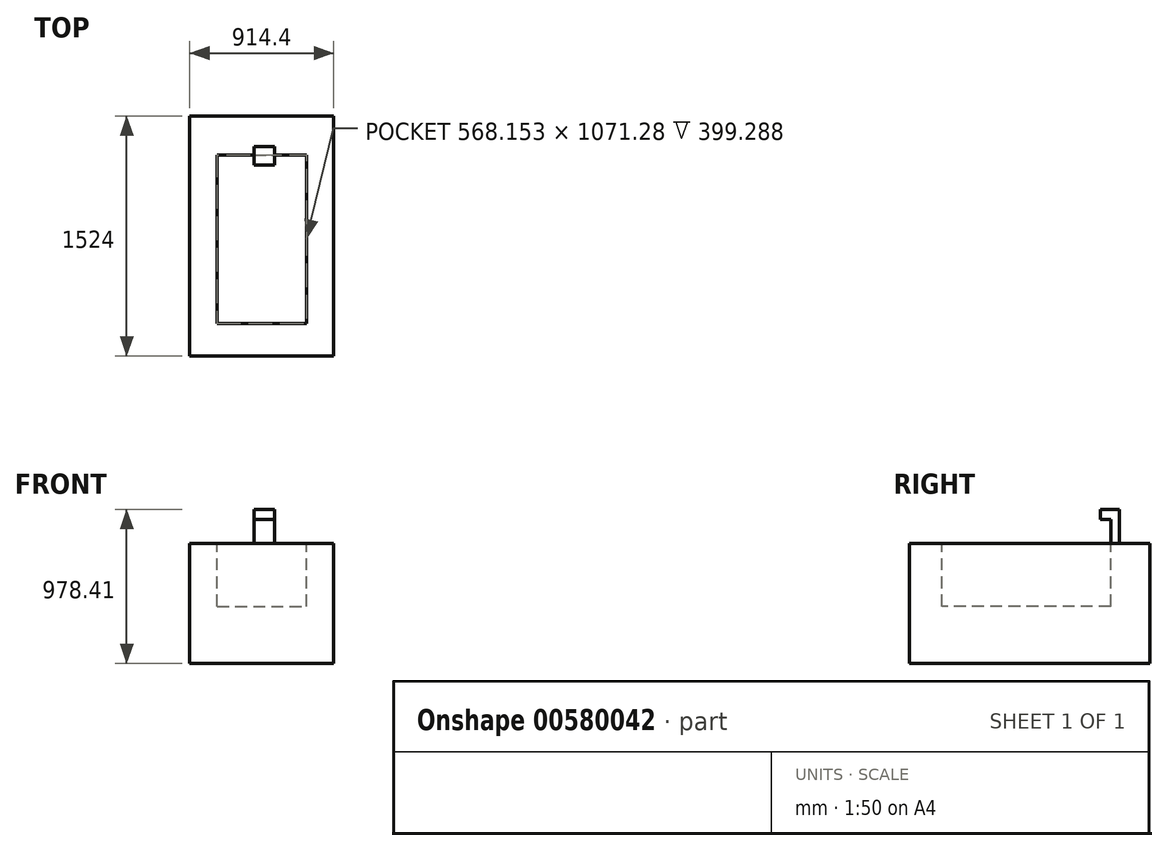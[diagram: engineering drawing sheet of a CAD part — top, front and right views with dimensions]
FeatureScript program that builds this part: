
annotation { "Feature Type Name" : "Feature", "Feature Type Description" : "" }
export const myFeature = defineFeature(function(context is Context, id is Id, definition is map)
    precondition{}
    {
        {
            var Q0;
            Q0=qCreatedBy(makeId("Top.planeOp"),FACE);
            var sketch = newSketch(context, id + "F0", { "sketchPlane" : qUnion([Q0])});
            skLineSegment(sketch, "E0.bottom", {"start": v(-580.76, 770.78) * mm, "end": v(333.64, 770.78) * mm});
            skLineSegment(sketch, "E0.top", {"start": v(-580.76, -753.22) * mm, "end": v(333.64, -753.22) * mm});
            skLineSegment(sketch, "E0.left", {"start": v(-580.76, 770.78) * mm, "end": v(-580.76, -753.22) * mm});
            skLineSegment(sketch, "E0.right", {"start": v(333.64, 770.78) * mm, "end": v(333.64, -753.22) * mm});
            skSolve(sketch);
        }
        {
            var Q0;
            Q0 = qSketchRegion(id + "F0", true);
            extrude(context, id + "F1", {"entities" : qUnion([Q0]), "depth" : 762 * mm, "offsetDistance" : 30.48 * mm});
        }
        {
            var Q0;
            Q0=makeQuery(id+"F1.opExtrude","CAP_FACE",FACE,{"disambiguationData":[OSD([sQuery(id+"F0.wireOp",EDGE,"E0.bottom"),sQuery(id+"F0.wireOp",EDGE,"E0.top"),sQuery(id+"F0.wireOp",EDGE,"E0.left"),sQuery(id+"F0.wireOp",EDGE,"E0.right")])],"isStart":false});
            var sketch = newSketch(context, id + "F2", { "sketchPlane" : qUnion([Q0])});
            skLineSegment(sketch, "E1.bottom", {"start": v(-407.14, 523.6) * mm, "end": v(161.01, 523.6) * mm});
            skLineSegment(sketch, "E1.top", {"start": v(-407.14, -547.67) * mm, "end": v(161.01, -547.67) * mm});
            skLineSegment(sketch, "E1.left", {"start": v(-407.14, 523.6) * mm, "end": v(-407.14, -547.67) * mm});
            skLineSegment(sketch, "E1.right", {"start": v(161.01, 523.6) * mm, "end": v(161.01, -547.67) * mm});
            skSolve(sketch);
        }
        {
            var Q0;
            Q0 = qSketchRegion(id + "F2", true);
            extrude(context, id + "F3", {"entities" : qUnion([Q0]), "operationType" : NewBodyOperationType.REMOVE, "oppositeDirection" : true, "depth" : 399.3 * mm, "offsetDistance" : 30.48 * mm});
        }
        {
            var Q0;
            Q0=makeQuery(id+"F1.opExtrude","CAP_FACE",FACE,{"disambiguationData":[OSD([sQuery(id+"F0.wireOp",EDGE,"E0.bottom"),sQuery(id+"F0.wireOp",EDGE,"E0.top"),sQuery(id+"F0.wireOp",EDGE,"E0.left"),sQuery(id+"F0.wireOp",EDGE,"E0.right")])],"isStart":false});
            var sketch = newSketch(context, id + "F4", { "sketchPlane" : qUnion([Q0])});
            skLineSegment(sketch, "E2.bottom", {"start": v(-171.47, 578.34) * mm, "end": v(-41.9, 578.34) * mm});
            skLineSegment(sketch, "E2.top", {"start": v(-171.47, 523.6) * mm, "end": v(-41.9, 523.6) * mm});
            skLineSegment(sketch, "E2.left", {"start": v(-171.47, 578.34) * mm, "end": v(-171.47, 523.6) * mm});
            skLineSegment(sketch, "E2.right", {"start": v(-41.9, 578.34) * mm, "end": v(-41.9, 523.6) * mm});
            skSolve(sketch);
        }
        {
            var Q0;
            Q0 = qSketchRegion(id + "F4", true);
            extrude(context, id + "F5", {"entities" : qUnion([Q0]), "operationType" : NewBodyOperationType.ADD, "depth" : 216.4 * mm, "offsetDistance" : 30.48 * mm});
        }
        {
            var Q0;
            Q0=makeQuery(id+"F5.boolean.opBoolean","MERGE",FACE,{"derivedFrom":[makeQuery(id+"F3.boolean.opBoolean","COPY",FACE,{"derivedFrom":makeQuery(id+"F3.opExtrude","SWEPT_FACE",FACE,{"disambiguationData":[OSD([sQuery(id+"F2.wireOp",EDGE,"E1.bottom")])]})}),makeQuery(id+"F5.opExtrude","SWEPT_FACE",FACE,{"disambiguationData":[OSD([sQuery(id+"F4.wireOp",EDGE,"E2.top")])]})]});
            var sketch = newSketch(context, id + "F6", { "sketchPlane" : qUnion([Q0])});
            skLineSegment(sketch, "E3.bottom", {"start": v(-171.47, 978.4) * mm, "end": v(-41.9, 978.4) * mm});
            skLineSegment(sketch, "E3.top", {"start": v(-171.47, 916.49) * mm, "end": v(-41.9, 916.49) * mm});
            skLineSegment(sketch, "E3.left", {"start": v(-171.47, 978.4) * mm, "end": v(-171.47, 916.49) * mm});
            skLineSegment(sketch, "E3.right", {"start": v(-41.9, 978.4) * mm, "end": v(-41.9, 916.49) * mm});
            skSolve(sketch);
        }
        {
            var Q0;
            Q0 = qSketchRegion(id + "F6", true);
            extrude(context, id + "F7", {"entities" : qUnion([Q0]), "operationType" : NewBodyOperationType.ADD, "depth" : 64 * mm, "offsetDistance" : 30.48 * mm});
        }
    });
